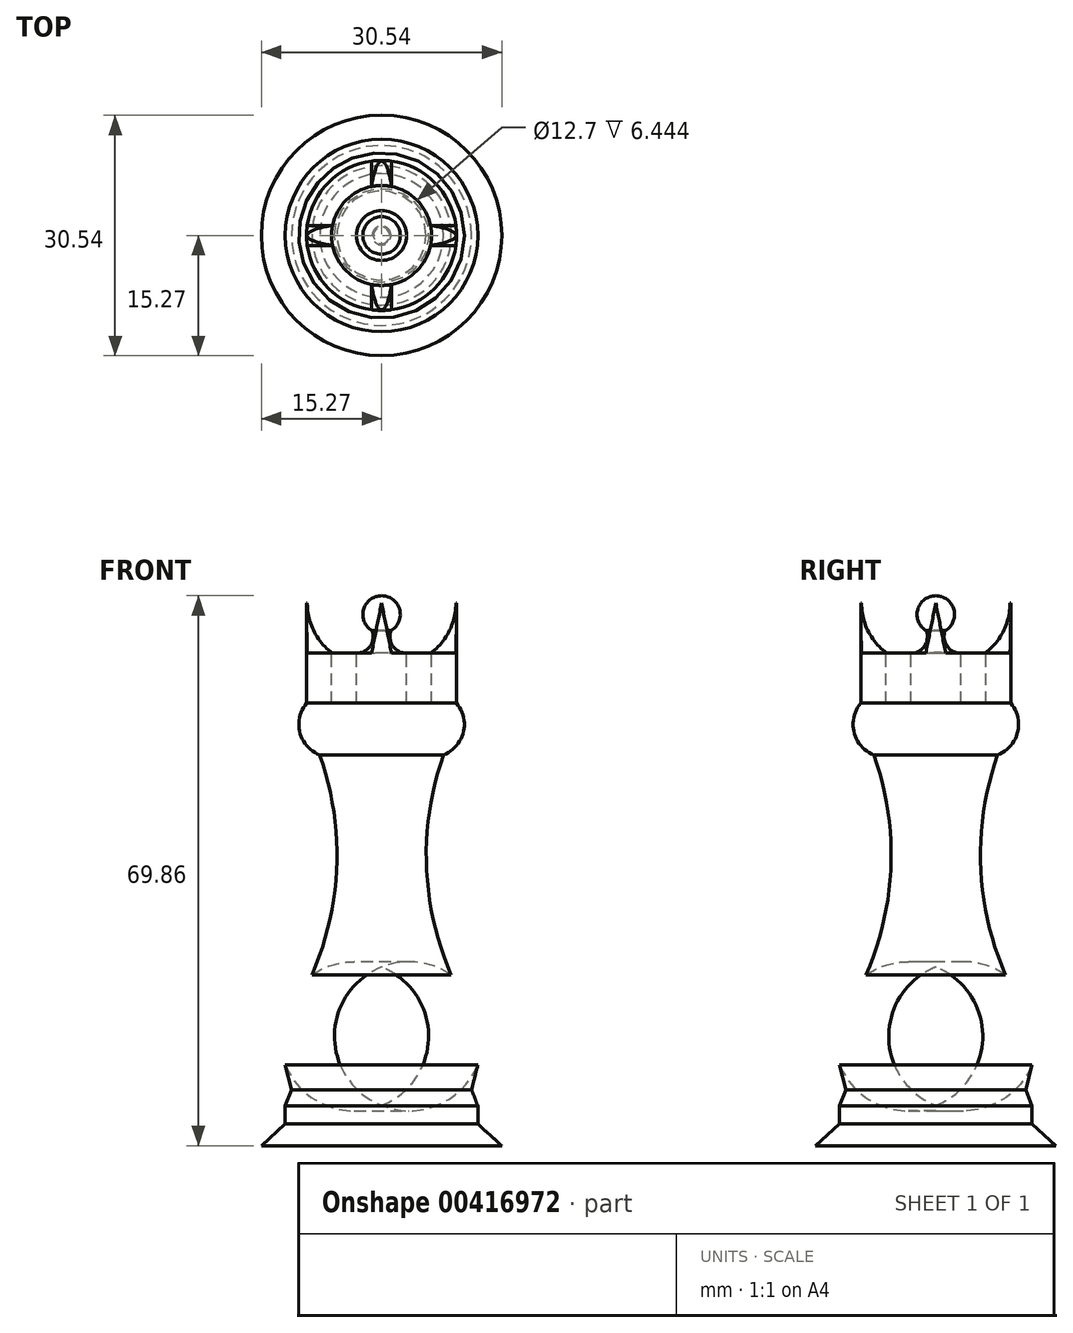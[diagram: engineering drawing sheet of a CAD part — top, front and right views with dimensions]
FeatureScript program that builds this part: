
annotation { "Feature Type Name" : "Feature", "Feature Type Description" : "" }
export const myFeature = defineFeature(function(context is Context, id is Id, definition is map)
    precondition{}
    {
        {
            var Q0;
            Q0=qCreatedBy(makeId("Front.planeOp"),FACE);
            var sketch = newSketch(context, id + "F0", { "sketchPlane" : qUnion([Q0])});
            skArc(sketch, "E0", {"start": v(7.85, 49.63) * mm, "mid": v(5.7, 35.57) * mm, "end": v(8.85, 21.7) * mm});
            skArc(sketch, "E1", {"start": v(7.85, 49.63) * mm, "mid": v(10.38, 52.49) * mm, "end": v(9.53, 56.2) * mm});
            skLineSegment(sketch, "E2", {"start": v(9.53, 56.2) * mm, "end": v(9.53, 62.56) * mm});
            skLineSegment(sketch, "E3", {"start": v(9.53, 62.56) * mm, "end": v(6.35, 62.56) * mm});
            skLineSegment(sketch, "E4", {"start": v(6.35, 62.56) * mm, "end": v(6.35, 56.2) * mm});
            skLineSegment(sketch, "E5", {"start": v(6.35, 56.2) * mm, "end": v(3.18, 56.2) * mm});
            skLineSegment(sketch, "E6", {"start": v(3.18, 56.2) * mm, "end": v(3.18, 62.56) * mm});
            skLineSegment(sketch, "E7", {"start": v(3.18, 62.56) * mm, "end": v(0, 62.56) * mm});
            skLineSegment(sketch, "E8", {"start": v(0, 62.56) * mm, "end": v(0, 56.2) * mm});
            skLineSegment(sketch, "E9", {"start": v(0, 56.2) * mm, "end": v(0, 21.7) * mm});
            skLineSegment(sketch, "E10", {"start": v(0, 21.7) * mm, "end": v(8.85, 21.7) * mm});
            skArc(sketch, "E11", {"start": v(12.23, 10.25) * mm, "mid": v(12.57, 16.58) * mm, "end": v(8.85, 21.7) * mm});
            skLineSegment(sketch, "E12", {"start": v(12.23, 10.25) * mm, "end": v(11.43, 7.1) * mm});
            skLineSegment(sketch, "E13", {"start": v(11.43, 7.1) * mm, "end": v(12.23, 5.06) * mm});
            skLineSegment(sketch, "E14", {"start": v(12.23, 5.06) * mm, "end": v(12.23, 2.74) * mm});
            skLineSegment(sketch, "E15", {"start": v(12.23, 2.74) * mm, "end": v(15.27, 0) * mm});
            skLineSegment(sketch, "E16", {"start": v(15.27, 0) * mm, "end": v(0, 0) * mm});
            skLineSegment(sketch, "E17", {"start": v(0, 0) * mm, "end": v(0, 21.7) * mm});
            skLineSegment(sketch, "E18", {"start": v(0, 65.1) * mm, "end": v(0, 69.86) * mm});
            skArc(sketch, "E19", {"start": v(0, 65.1) * mm, "mid": v(2.38, 67.48) * mm, "end": v(0, 69.86) * mm});
            skLineSegment(sketch, "E20", {"start": v(0, 67.48) * mm, "end": v(1.2, 65.42) * mm});
            skArc(sketch, "E21", {"start": v(1.2, 65.42) * mm, "mid": v(1.43, 63.47) * mm, "end": v(3.18, 62.56) * mm});
            skLineSegment(sketch, "E22", {"start": v(0, 65.1) * mm, "end": v(0, 62.56) * mm});
            skSolve(sketch);
        }
        {
            var Q0;
            Q0=makeQuery(id+"F0.imprint","IMPRINT",FACE,{"disambiguationData":[TD([[makeQuery(id+"F0.imprint","IMPRINT",EDGE,{"derivedFrom":sQuery(id+"F0.wireOp",EDGE,"E10")}),-1.0]])]});
            var Q1;
            Q1=makeQuery(id+"F0.imprint","IMPRINT",FACE,{"disambiguationData":[TD([[makeQuery(id+"F0.imprint","IMPRINT",EDGE,{"derivedFrom":sQuery(id+"F0.wireOp",EDGE,"E0")}),-1.0]])]});
            var Q2;
            Q2=makeQuery(id+"F0.imprint","IMPRINT",FACE,{"disambiguationData":[TD([[makeQuery(id+"F0.imprint","IMPRINT",EDGE,{"derivedFrom":sQuery(id+"F0.wireOp",EDGE,"E4")}),-1.0]])]});
            var Q3;
            Q3=sQuery(id+"F0.wireOp",EDGE,"E9");
            revolve(context, id + "F1", {"entities" : qUnion([Q0, Q1, Q2]), "axis" : qUnion([Q3]), "revolveType" : RevolveType.FULL});
        }
        {
            var Q0;
            Q0=makeQuery(id+"F1.opRevolve","SWEPT_FACE",FACE,{"disambiguationData":[OSD([sQuery(id+"F0.wireOp",EDGE,"E3")])]});
            var sketch = newSketch(context, id + "F2", { "sketchPlane" : qUnion([Q0])});
            skLineSegment(sketch, "E23", {"start": v(0, 0) * mm, "end": v(0, -9.53) * mm});
            skLineSegment(sketch, "E24", {"start": v(0, 0) * mm, "end": v(9.53, 0) * mm});
            skLineSegment(sketch, "E25", {"start": v(0, 0) * mm, "end": v(-9.53, 0) * mm});
            skLineSegment(sketch, "E26", {"start": v(0, 0) * mm, "end": v(0, 9.53) * mm});
            skCircle(sketch, "E27", {"center": v(0, 0) * mm, "radius": 9.53 * mm});
            skCircle(sketch, "E28", {"center": v(0, 0) * mm, "radius": 6.35 * mm});
            skLineSegment(sketch, "E29", {"start": v(-9.44, 1.27) * mm, "end": v(-6.22, 1.27) * mm});
            skLineSegment(sketch, "E30", {"start": v(-9.44, -1.27) * mm, "end": v(-6.22, -1.27) * mm});
            skLineSegment(sketch, "E31", {"start": v(6.22, 1.27) * mm, "end": v(9.44, 1.27) * mm});
            skLineSegment(sketch, "E32", {"start": v(6.22, -1.27) * mm, "end": v(9.44, -1.27) * mm});
            skLineSegment(sketch, "E33", {"start": v(1.27, -6.22) * mm, "end": v(1.27, -9.44) * mm});
            skLineSegment(sketch, "E34", {"start": v(-1.27, -6.22) * mm, "end": v(-1.27, -9.44) * mm});
            skLineSegment(sketch, "E35", {"start": v(-1.27, 6.22) * mm, "end": v(-1.27, 9.44) * mm});
            skLineSegment(sketch, "E36", {"start": v(1.27, 9.44) * mm, "end": v(1.27, 6.22) * mm});
            skSolve(sketch);
        }
        {
            var Q0;
            {var subQ5=sQuery(id+"F2.wireOp",EDGE,"E29");Q0=makeQuery(id+"F2.imprint","IMPRINT",FACE,{"disambiguationData":[TD([[makeQuery(id+"F2.imprint","IMPRINT",EDGE,{"derivedFrom":subQ5}),-1.0]])]});}
            var Q1;
            {var subQ5=sQuery(id+"F2.wireOp",EDGE,"E30");Q1=makeQuery(id+"F2.imprint","IMPRINT",FACE,{"disambiguationData":[TD([[makeQuery(id+"F2.imprint","IMPRINT",EDGE,{"derivedFrom":subQ5}),1.0]])]});}
            var Q2;
            {var subQ5=sQuery(id+"F2.wireOp",EDGE,"E34");Q2=makeQuery(id+"F2.imprint","IMPRINT",FACE,{"disambiguationData":[TD([[makeQuery(id+"F2.imprint","IMPRINT",EDGE,{"derivedFrom":subQ5}),1.0]])]});}
            var Q3;
            {var subQ5=sQuery(id+"F2.wireOp",EDGE,"E33");Q3=makeQuery(id+"F2.imprint","IMPRINT",FACE,{"disambiguationData":[TD([[makeQuery(id+"F2.imprint","IMPRINT",EDGE,{"derivedFrom":subQ5}),-1.0]])]});}
            var Q4;
            {var subQ5=sQuery(id+"F2.wireOp",EDGE,"E31");Q4=makeQuery(id+"F2.imprint","IMPRINT",FACE,{"disambiguationData":[TD([[makeQuery(id+"F2.imprint","IMPRINT",EDGE,{"derivedFrom":subQ5}),-1.0]])]});}
            var Q5;
            {var subQ5=sQuery(id+"F2.wireOp",EDGE,"E32");Q5=makeQuery(id+"F2.imprint","IMPRINT",FACE,{"disambiguationData":[TD([[makeQuery(id+"F2.imprint","IMPRINT",EDGE,{"derivedFrom":subQ5}),1.0]])]});}
            var Q6;
            {var subQ5=sQuery(id+"F2.wireOp",EDGE,"E36");Q6=makeQuery(id+"F2.imprint","IMPRINT",FACE,{"disambiguationData":[TD([[makeQuery(id+"F2.imprint","IMPRINT",EDGE,{"derivedFrom":subQ5}),-1.0]])]});}
            var Q7;
            {var subQ5=sQuery(id+"F2.wireOp",EDGE,"E35");Q7=makeQuery(id+"F2.imprint","IMPRINT",FACE,{"disambiguationData":[TD([[makeQuery(id+"F2.imprint","IMPRINT",EDGE,{"derivedFrom":subQ5}),-1.0]])]});}
            extrude(context, id + "F3", {"entities" : qUnion([Q0, Q1, Q2, Q3, Q4, Q5, Q6, Q7]), "operationType" : NewBodyOperationType.ADD, "depth" : 6.35 * mm, "offsetDistance" : 25.4 * mm});
        }
        {
            var Q0;
            Q0=makeQuery(id+"F3.opExtrude","SWEPT_FACE",FACE,{"disambiguationData":[OSD([sQuery(id+"F2.wireOp",EDGE,"E30")])]});
            var sketch = newSketch(context, id + "F4", { "sketchPlane" : qUnion([Q0])});
            skArc(sketch, "E37", {"start": v(-9.44, 68.9) * mm, "mid": v(-8.59, 65.35) * mm, "end": v(-6.22, 62.56) * mm});
            skLineSegment(sketch, "E38", {"start": v(-9.44, 68.9) * mm, "end": v(-6.22, 68.9) * mm});
            skLineSegment(sketch, "E39", {"start": v(-6.22, 68.9) * mm, "end": v(-6.22, 62.56) * mm});
            skSolve(sketch);
        }
        {
            var Q0;
            Q0=makeQuery(id+"F3.opExtrude","SWEPT_FACE",FACE,{"disambiguationData":[OSD([sQuery(id+"F2.wireOp",EDGE,"E32")])]});
            var sketch = newSketch(context, id + "F5", { "sketchPlane" : qUnion([Q0])});
            skArc(sketch, "E40", {"start": v(6.22, 62.56) * mm, "mid": v(8.59, 65.35) * mm, "end": v(9.44, 68.9) * mm});
            skLineSegment(sketch, "E41", {"start": v(6.22, 68.9) * mm, "end": v(6.22, 62.56) * mm});
            skLineSegment(sketch, "E42", {"start": v(6.22, 68.9) * mm, "end": v(9.44, 68.9) * mm});
            skSolve(sketch);
        }
        {
            var Q0;
            Q0=makeQuery(id+"F4.imprint","IMPRINT",FACE,{"disambiguationData":[TD([[makeQuery(id+"F4.imprint","IMPRINT",EDGE,{"derivedFrom":sQuery(id+"F4.wireOp",EDGE,"E37")}),1.0]])]});
            var Q1;
            Q1=makeQuery(id+"F5.imprint","IMPRINT",FACE,{"disambiguationData":[TD([[makeQuery(id+"F5.imprint","IMPRINT",EDGE,{"derivedFrom":sQuery(id+"F5.wireOp",EDGE,"E40")}),1.0]])]});
            extrude(context, id + "F6", {"entities" : qUnion([Q0, Q1]), "operationType" : NewBodyOperationType.REMOVE, "oppositeDirection" : true, "depth" : 25.4 * mm, "offsetDistance" : 25.4 * mm});
        }
        {
            var Q0;
            Q0=makeQuery(id+"F3.opExtrude","SWEPT_FACE",FACE,{"disambiguationData":[OSD([sQuery(id+"F2.wireOp",EDGE,"E33")])]});
            var sketch = newSketch(context, id + "F7", { "sketchPlane" : qUnion([Q0])});
            skArc(sketch, "E43", {"start": v(-9.44, 68.9) * mm, "mid": v(-8.59, 65.35) * mm, "end": v(-6.22, 62.56) * mm});
            skLineSegment(sketch, "E44", {"start": v(-9.44, 68.9) * mm, "end": v(-6.22, 68.9) * mm});
            skLineSegment(sketch, "E45", {"start": v(-6.22, 68.9) * mm, "end": v(-6.22, 62.56) * mm});
            skSolve(sketch);
        }
        {
            var Q0;
            Q0=makeQuery(id+"F3.opExtrude","SWEPT_FACE",FACE,{"disambiguationData":[OSD([sQuery(id+"F2.wireOp",EDGE,"E36")])]});
            var sketch = newSketch(context, id + "F8", { "sketchPlane" : qUnion([Q0])});
            skArc(sketch, "E46", {"start": v(6.22, 62.56) * mm, "mid": v(8.59, 65.35) * mm, "end": v(9.44, 68.9) * mm});
            skLineSegment(sketch, "E47", {"start": v(6.22, 68.9) * mm, "end": v(6.22, 62.56) * mm});
            skLineSegment(sketch, "E48", {"start": v(6.22, 68.9) * mm, "end": v(9.44, 68.9) * mm});
            skSolve(sketch);
        }
        {
            var Q0;
            Q0=makeQuery(id+"F7.imprint","IMPRINT",FACE,{"disambiguationData":[TD([[makeQuery(id+"F7.imprint","IMPRINT",EDGE,{"derivedFrom":sQuery(id+"F7.wireOp",EDGE,"E43")}),1.0]])]});
            var Q1;
            Q1=makeQuery(id+"F8.imprint","IMPRINT",FACE,{"disambiguationData":[TD([[makeQuery(id+"F8.imprint","IMPRINT",EDGE,{"derivedFrom":sQuery(id+"F8.wireOp",EDGE,"E46")}),1.0]])]});
            extrude(context, id + "F9", {"entities" : qUnion([Q0, Q1]), "operationType" : NewBodyOperationType.REMOVE, "oppositeDirection" : true, "depth" : 25.4 * mm, "offsetDistance" : 25.4 * mm});
        }
        {
            var Q0;
            Q0=qCreatedBy(makeId("Front.planeOp"),FACE);
            cPlane(context, id + "F10", {"entities" : qUnion([Q0]), "cplaneType" : CPlaneType.OFFSET, "offset" : 9.52 * mm, "width" : 152.4 * mm, "height" : 152.4 * mm});
        }
        {
            var Q0;
            Q0=qCreatedBy(id+"F10.planeOp",FACE);
            var sketch = newSketch(context, id + "F11", { "sketchPlane" : qUnion([Q0])});
            skLineSegment(sketch, "E49.bottom", {"start": v(-1.27, 68.9) * mm, "end": v(1.27, 68.9) * mm});
            skLineSegment(sketch, "E49.top", {"start": v(-1.27, 62.56) * mm, "end": v(1.27, 62.56) * mm});
            skLineSegment(sketch, "E49.left", {"start": v(-1.27, 68.9) * mm, "end": v(-1.27, 62.56) * mm});
            skLineSegment(sketch, "E49.right", {"start": v(1.27, 68.9) * mm, "end": v(1.27, 62.56) * mm});
            skLineSegment(sketch, "E50", {"start": v(0, 68.9) * mm, "end": v(0, 62.56) * mm});
            skLineSegment(sketch, "E51", {"start": v(0, 68.9) * mm, "end": v(-1.27, 62.56) * mm});
            skLineSegment(sketch, "E52", {"start": v(0, 68.9) * mm, "end": v(1.27, 62.56) * mm});
            skSolve(sketch);
        }
        {
            var Q0;
            {var subQ0=sQuery(id+"F11.wireOp",EDGE,"E49.left");Q0=makeQuery(id+"F11.imprint","IMPRINT",FACE,{"disambiguationData":[TD([[makeQuery(id+"F11.imprint","IMPRINT",EDGE,{"derivedFrom":subQ0}),1.0]])]});}
            var Q1;
            {var subQ0=sQuery(id+"F11.wireOp",EDGE,"E49.right");Q1=makeQuery(id+"F11.imprint","IMPRINT",FACE,{"disambiguationData":[TD([[makeQuery(id+"F11.imprint","IMPRINT",EDGE,{"derivedFrom":subQ0}),-1.0]])]});}
            extrude(context, id + "F12", {"entities" : qUnion([Q0, Q1]), "operationType" : NewBodyOperationType.REMOVE, "oppositeDirection" : true, "depth" : 25.4 * mm, "offsetDistance" : 25.4 * mm});
        }
        {
            var Q0;
            Q0=qCreatedBy(makeId("Right.planeOp"),FACE);
            cPlane(context, id + "F13", {"entities" : qUnion([Q0]), "cplaneType" : CPlaneType.OFFSET, "offset" : 9.52 * mm, "width" : 152.4 * mm, "height" : 152.4 * mm});
        }
        {
            var Q0;
            Q0=qCreatedBy(id+"F13.planeOp",FACE);
            var sketch = newSketch(context, id + "F14", { "sketchPlane" : qUnion([Q0])});
            skLineSegment(sketch, "E53.bottom", {"start": v(-1.27, 68.9) * mm, "end": v(1.27, 68.9) * mm});
            skLineSegment(sketch, "E53.top", {"start": v(-1.27, 62.56) * mm, "end": v(1.27, 62.56) * mm});
            skLineSegment(sketch, "E53.left", {"start": v(-1.27, 68.9) * mm, "end": v(-1.27, 62.56) * mm});
            skLineSegment(sketch, "E53.right", {"start": v(1.27, 68.9) * mm, "end": v(1.27, 62.56) * mm});
            skLineSegment(sketch, "E54", {"start": v(0, 68.9) * mm, "end": v(0, 62.56) * mm});
            skLineSegment(sketch, "E55", {"start": v(-1.27, 62.56) * mm, "end": v(0, 68.9) * mm});
            skLineSegment(sketch, "E56", {"start": v(0, 68.9) * mm, "end": v(1.27, 62.56) * mm});
            skSolve(sketch);
        }
        {
            var Q0;
            {var subQ0=sQuery(id+"F14.wireOp",EDGE,"E53.right");Q0=makeQuery(id+"F14.imprint","IMPRINT",FACE,{"disambiguationData":[TD([[makeQuery(id+"F14.imprint","IMPRINT",EDGE,{"derivedFrom":subQ0}),-1.0]])]});}
            var Q1;
            {var subQ0=sQuery(id+"F14.wireOp",EDGE,"E53.left");Q1=makeQuery(id+"F14.imprint","IMPRINT",FACE,{"disambiguationData":[TD([[makeQuery(id+"F14.imprint","IMPRINT",EDGE,{"derivedFrom":subQ0}),1.0]])]});}
            extrude(context, id + "F15", {"entities" : qUnion([Q0, Q1]), "operationType" : NewBodyOperationType.REMOVE, "oppositeDirection" : true, "depth" : 25.4 * mm, "offsetDistance" : 25.4 * mm});
        }
        {
            var Q0;
            Q0=makeQuery(id+"F0.imprint","IMPRINT",FACE,{"disambiguationData":[TD([[makeQuery(id+"F0.imprint","IMPRINT",EDGE,{"derivedFrom":sQuery(id+"F0.wireOp",EDGE,"E7")}),-1.0]])]});
            var Q1;
            {var subQ3=sQuery(id+"F0.wireOp",EDGE,"E20");Q1=makeQuery(id+"F0.imprint","IMPRINT",FACE,{"disambiguationData":[TD([[makeQuery(id+"F0.imprint","IMPRINT",EDGE,{"derivedFrom":subQ3}),1.0]])]});}
            var Q2;
            {var subQ3=sQuery(id+"F0.wireOp",EDGE,"E20");Q2=makeQuery(id+"F0.imprint","IMPRINT",FACE,{"disambiguationData":[TD([[makeQuery(id+"F0.imprint","IMPRINT",EDGE,{"derivedFrom":subQ3}),-1.0]])]});}
            var Q3;
            Q3=sQuery(id+"F0.wireOp",EDGE,"E22");
            revolve(context, id + "F16", {"operationType" : NewBodyOperationType.ADD, "entities" : qUnion([Q0, Q1, Q2]), "axis" : qUnion([Q3]), "revolveType" : RevolveType.FULL});
        }
    });
